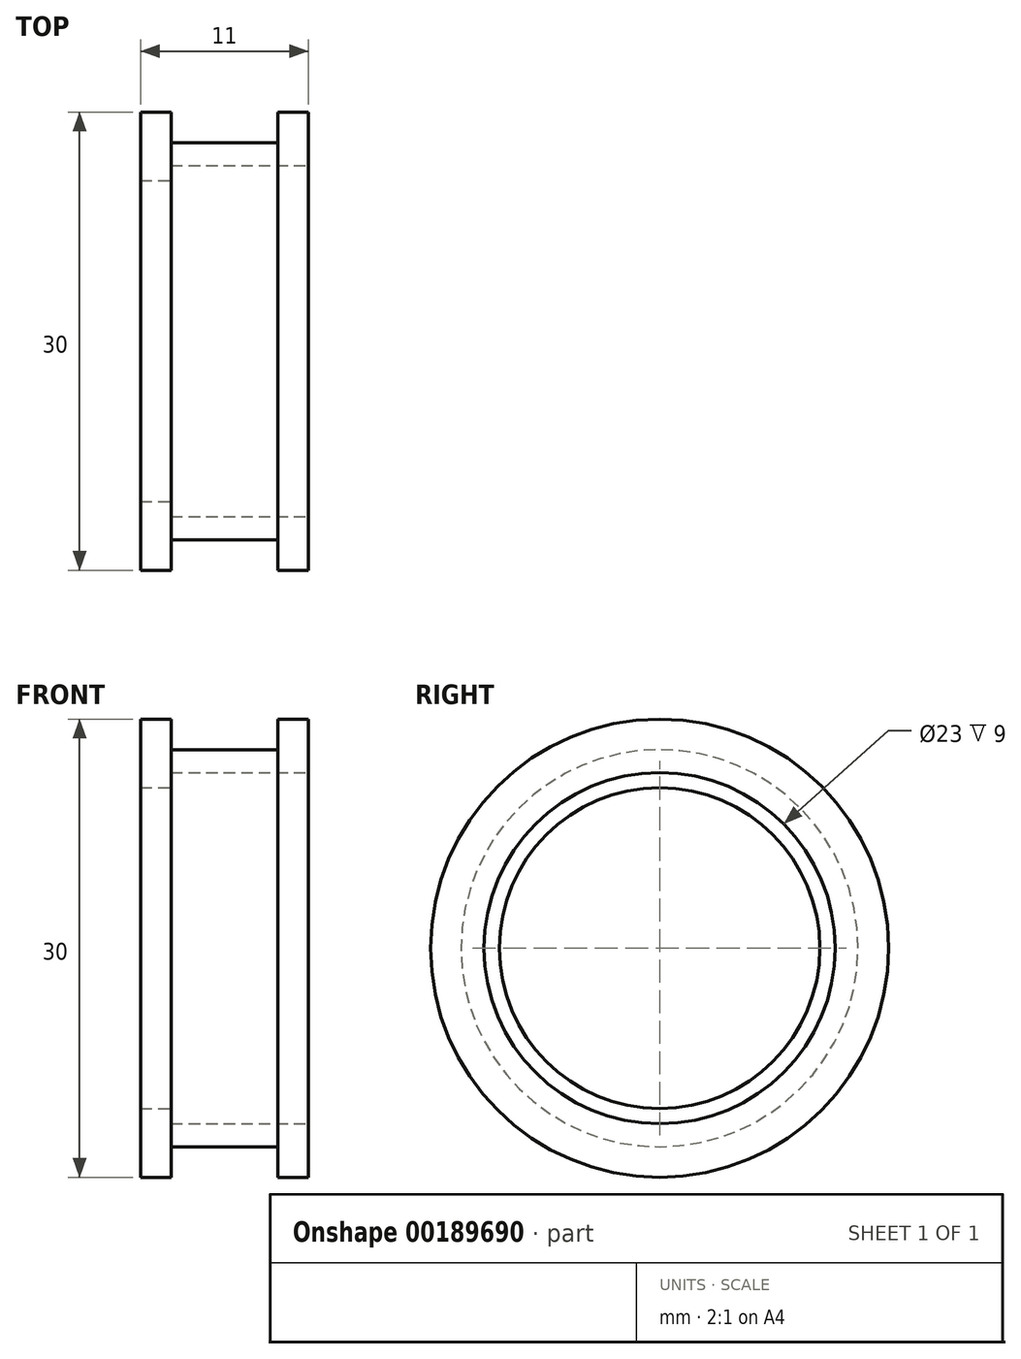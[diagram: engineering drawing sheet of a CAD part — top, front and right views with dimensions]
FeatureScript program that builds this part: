
annotation { "Feature Type Name" : "Feature", "Feature Type Description" : "" }
export const myFeature = defineFeature(function(context is Context, id is Id, definition is map)
    precondition{}
    {
        {
            var Q0;
            Q0=qCreatedBy(makeId("Front.planeOp"),FACE);
            var sketch = newSketch(context, id + "F0", { "sketchPlane" : qUnion([Q0])});
            skLineSegment(sketch, "E0", {"start": v(-5.5, 0) * mm, "end": v(-5.5, 15) * mm});
            skLineSegment(sketch, "E1", {"start": v(-5.5, 15) * mm, "end": v(-3.5, 15) * mm});
            skLineSegment(sketch, "E2", {"start": v(-3.5, 15) * mm, "end": v(-3.5, 13) * mm});
            skLineSegment(sketch, "E3", {"start": v(-3.5, 13) * mm, "end": v(3.5, 13) * mm});
            skLineSegment(sketch, "E4", {"start": v(3.5, 13) * mm, "end": v(3.5, 15) * mm});
            skLineSegment(sketch, "E5", {"start": v(3.5, 15) * mm, "end": v(5.5, 15) * mm});
            skLineSegment(sketch, "E6", {"start": v(5.5, 15) * mm, "end": v(5.5, 0) * mm});
            skPoint(sketch, "E7.orphan", {"position": v(5.5, 13) * mm});
            skPoint(sketch, "E8.orphan", {"position": v(-5.5, 13) * mm});
            skLineSegment(sketch, "E9", {"start": v(-5.5, 0) * mm, "end": v(5.5, 0) * mm});
            skPoint(sketch, "E10", {"position": v(0, 0) * mm});
            skSolve(sketch);
        }
        {
            var Q0;
            Q0 = qSketchRegion(id + "F0", true);
            var Q1;
            Q1=sQuery(id+"F0.wireOp",EDGE,"E9");
            revolve(context, id + "F1", {"surfaceOperationType" : NewSurfaceOperationType.NEW, "entities" : qUnion([Q0]), "axis" : qUnion([Q1]), "revolveType" : RevolveType.FULL});
        }
        {
            var Q0;
            Q0=makeQuery(id+"F1.opRevolve","SWEPT_FACE",FACE,{"disambiguationData":[OSD([sQuery(id+"F0.wireOp",EDGE,"E6")])]});
            var sketch = newSketch(context, id + "F2", { "sketchPlane" : qUnion([Q0])});
            skCircle(sketch, "E11", {"center": v(0, 0) * mm, "radius": 11.5 * mm});
            skCircle(sketch, "E12", {"center": v(0, 0) * mm, "radius": 10.5 * mm});
            skSolve(sketch);
        }
        {
            var Q0;
            Q0=makeQuery(id+"F2.imprint","IMPRINT",FACE,{"disambiguationData":[TD([[makeQuery(id+"F2.imprint","IMPRINT",EDGE,{"derivedFrom":sQuery(id+"F2.wireOp",EDGE,"E12")}),1.0]])]});
            extrude(context, id + "F3", {"entities" : qUnion([Q0]), "operationType" : NewBodyOperationType.REMOVE, "oppositeDirection" : true, "offsetDistance" : 25 * mm, "depth" : 25 * mm});
        }
        {
            var Q0;
            Q0=makeQuery(id+"F2.imprint","IMPRINT",FACE,{"disambiguationData":[TD([[makeQuery(id+"F2.imprint","IMPRINT",EDGE,{"derivedFrom":sQuery(id+"F2.wireOp",EDGE,"E11")}),1.0]])]});
            extrude(context, id + "F4", {"entities" : qUnion([Q0]), "operationType" : NewBodyOperationType.REMOVE, "oppositeDirection" : true, "offsetDistance" : 25 * mm, "depth" : 9 * mm});
        }
    });
